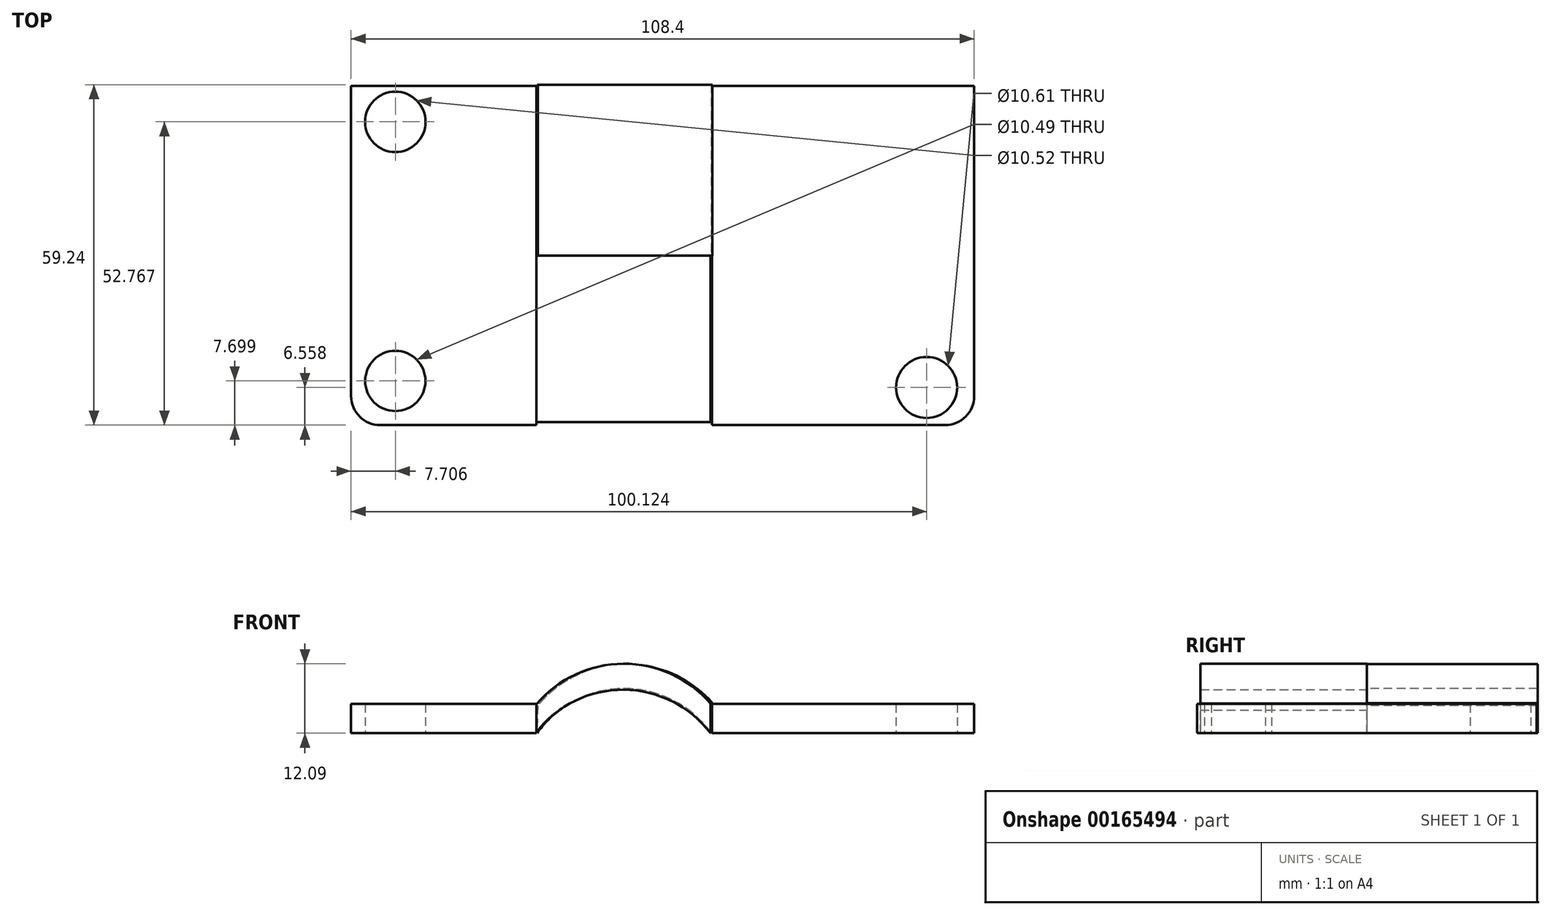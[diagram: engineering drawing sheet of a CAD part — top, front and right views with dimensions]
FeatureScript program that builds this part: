
annotation { "Feature Type Name" : "Feature", "Feature Type Description" : "" }
export const myFeature = defineFeature(function(context is Context, id is Id, definition is map)
    precondition{}
    {
        {
            var Q0;
            Q0=qCreatedBy(makeId("Top.planeOp"),FACE);
            var sketch = newSketch(context, id + "F0", { "sketchPlane" : qUnion([Q0])});
            skLineSegment(sketch, "E0.bottom", {"start": v(54.2, -29.52) * mm, "end": v(-54.2, -29.52) * mm});
            skLineSegment(sketch, "E0.top", {"start": v(54.2, 29.52) * mm, "end": v(-54.2, 29.52) * mm});
            skLineSegment(sketch, "E0.left", {"start": v(54.2, -29.52) * mm, "end": v(54.2, 29.52) * mm});
            skLineSegment(sketch, "E0.right", {"start": v(-54.2, -29.52) * mm, "end": v(-54.2, 29.52) * mm});
            skPoint(sketch, "E0.middle", {"position": v(0, 0) * mm});
            skCircle(sketch, "E1", {"center": v(-46.5, -21.82) * mm, "radius": 5.24 * mm});
            skCircle(sketch, "E2", {"center": v(-46.5, 23.25) * mm, "radius": 5.26 * mm});
            skCircle(sketch, "E3", {"center": v(45.92, -22.96) * mm, "radius": 5.3 * mm});
            skLineSegment(sketch, "E4", {"start": v(-21.96, 29.52) * mm, "end": v(-21.96, -29.52) * mm});
            skLineSegment(sketch, "E5", {"start": v(8.56, 29.52) * mm, "end": v(8.56, -29.52) * mm});
            skSolve(sketch);
        }
        {
            var Q0;
            {var subQ0=sQuery(id+"F0.wireOp",EDGE,"E0.right");Q0=makeQuery(id+"F0.imprint","IMPRINT",FACE,{"disambiguationData":[TD([[makeQuery(id+"F0.imprint","IMPRINT",EDGE,{"derivedFrom":subQ0}),-1.0]])]});}
            var Q1;
            {var subQ0=sQuery(id+"F0.wireOp",EDGE,"E0.left");Q1=makeQuery(id+"F0.imprint","IMPRINT",FACE,{"disambiguationData":[TD([[makeQuery(id+"F0.imprint","IMPRINT",EDGE,{"derivedFrom":subQ0}),1.0]])]});}
            extrude(context, id + "F1", {"entities" : qUnion([Q0, Q1]), "depth" : 5.08 * mm});
        }
        {
            var Q0;
            Q0=makeQuery(id+"F1.opExtrude","SWEPT_EDGE",EDGE,{"disambiguationData":[OSD([sQuery(id+"F0.wireOp",EDGE,"E0.bottom"),sQuery(id+"F0.wireOp",EDGE,"E0.right")])]});
            var Q1;
            Q1=makeQuery(id+"F1.opExtrude","SWEPT_EDGE",EDGE,{"disambiguationData":[OSD([sQuery(id+"F0.wireOp",EDGE,"E0.bottom"),sQuery(id+"F0.wireOp",EDGE,"E0.left")])]});
            fillet(context, id + "F2", {"entities" : qUnion([Q0, Q1]), "radius" : 5.08 * mm, "tangentPropagation" : true, "allowEdgeOverflow" : false});
        }
        {
            var Q0;
            Q0=qCreatedBy(makeId("Front.planeOp"),FACE);
            var sketch = newSketch(context, id + "F3", { "sketchPlane" : qUnion([Q0])});
            skArc(sketch, "E6", {"start": v(8.32, 0) * mm, "mid": v(-6.88, 7.56) * mm, "end": v(-22.1, 0) * mm});
            skArc(sketch, "E7", {"start": v(8.32, 5.18) * mm, "mid": v(-6.84, 12.09) * mm, "end": v(-21.93, 5.02) * mm});
            skLineSegment(sketch, "E8", {"start": v(-21.93, 5.02) * mm, "end": v(-22.1, 0) * mm});
            skLineSegment(sketch, "E9", {"start": v(8.32, 5.18) * mm, "end": v(8.32, 0) * mm});
            skSolve(sketch);
        }
        {
            var Q0;
            Q0=makeQuery(id+"F3.imprint","IMPRINT",FACE,{"disambiguationData":[TD([[makeQuery(id+"F3.imprint","IMPRINT",EDGE,{"derivedFrom":sQuery(id+"F3.wireOp",EDGE,"E6")}),-1.0]])]});
            extrude(context, id + "F4", {"entities" : qUnion([Q0]), "operationType" : NewBodyOperationType.ADD, "depth" : 28.96 * mm});
        }
        {
            var Q0;
            Q0=qCreatedBy(makeId("Front.planeOp"),FACE);
            var sketch = newSketch(context, id + "F5", { "sketchPlane" : qUnion([Q0])});
            skArc(sketch, "E10", {"start": v(8.66, 5.23) * mm, "mid": v(-6.62, 12.02) * mm, "end": v(-21.7, 4.81) * mm});
            skArc(sketch, "E11", {"start": v(8.49, 0) * mm, "mid": v(-6.7, 7.78) * mm, "end": v(-21.87, 0) * mm});
            skLineSegment(sketch, "E12", {"start": v(8.66, 5.23) * mm, "end": v(8.49, 0) * mm});
            skLineSegment(sketch, "E13", {"start": v(-21.7, 4.81) * mm, "end": v(-21.87, -0.62) * mm});
            skSolve(sketch);
        }
        {
            var Q0;
            {var subQ0=sQuery(id+"F5.wireOp",EDGE,"E10");Q0=makeQuery(id+"F5.imprint","IMPRINT",FACE,{"disambiguationData":[TD([[makeQuery(id+"F5.imprint","IMPRINT",EDGE,{"derivedFrom":subQ0}),1.0]])]});}
            extrude(context, id + "F6", {"entities" : qUnion([Q0]), "oppositeDirection" : true, "depth" : 29.72 * mm});
        }
    });
